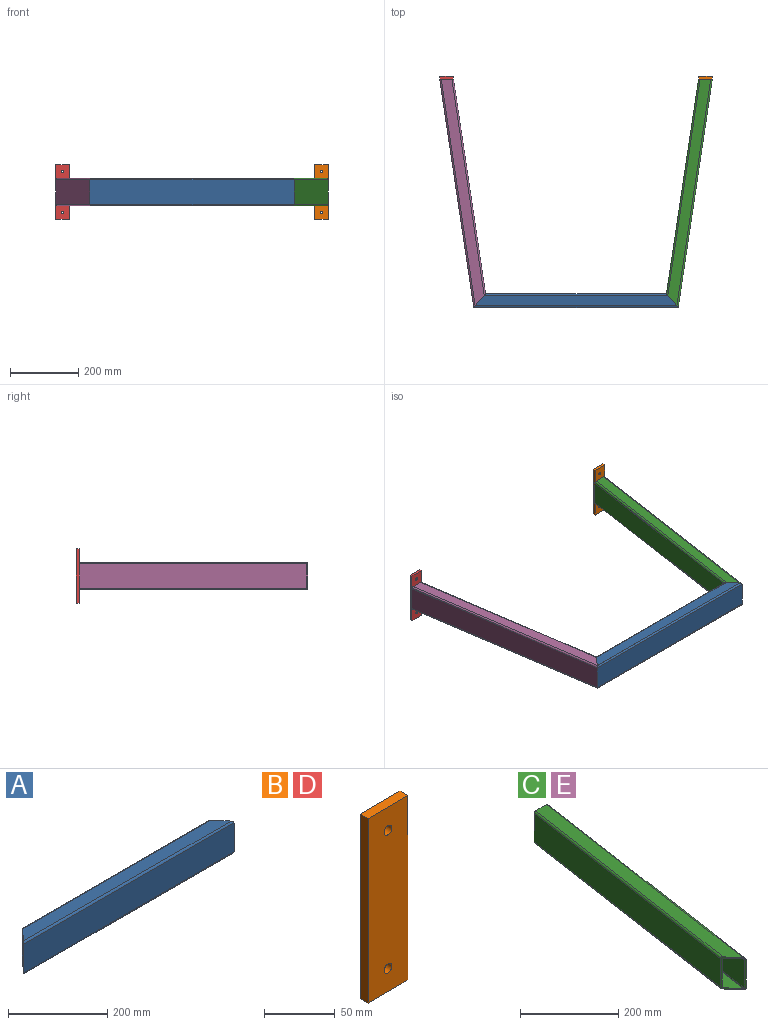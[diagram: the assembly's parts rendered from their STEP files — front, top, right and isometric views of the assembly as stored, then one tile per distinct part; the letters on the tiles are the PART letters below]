
ASSEMBLY  parts=5 mates=2
PART A: 18 faces, bbox 600x40x80 mm
  f0: cylinder r=4.5mm len=600mm, axis (-1,0,0), area 4221.2mm2, adj f2,f7,f8,f17
  f1: cylinder r=4.5mm len=600mm, axis (1,0,0), area 4221.2mm2, adj f2,f6,f8,f17
  f2: plane 600x71mm, normal (0,-1,0), area 42600mm2, adj f0,f1,f8,f17
  f3: cylinder r=4.5mm len=538.81mm, axis (1,0,0), area 3773.7mm2, adj f5,f7,f8,f17
  f4: cylinder r=4.5mm len=538.81mm, axis (-1,0,0), area 3773.7mm2, adj f5,f6,f8,f17
  f5: plane 531.05x71mm, normal (0,1,0), area 37704.8mm2, adj f3,f4,f8,f17
  f6: plane 592.24x31mm, normal (0,0,-1), area 17531.3mm2, adj f1,f4,f8,f17
  f7: plane 592.24x31mm, normal (0,0,1), area 17531.3mm2, adj f0,f3,f8,f17
  f8: plane 80x40mm, normal (-0.76,0.65,0), area 882.6mm2, adj f0,f1,f2,f3,f4,f5,f6,f7
  f9: cylinder r=1.5mm len=594.83mm, axis (1,0,0), area 1399.3mm2, adj f8,f11,f15,f17
  f10: cylinder r=1.5mm len=594.83mm, axis (-1,0,0), area 1399.3mm2, adj f8,f11,f16,f17
  f11: plane 594.83x71mm, normal (0,1,0), area 42232.9mm2, adj f8,f9,f10,f17
  f12: cylinder r=1.5mm len=538.81mm, axis (-1,0,0), area 1265.7mm2, adj f8,f14,f15,f17
  f13: cylinder r=1.5mm len=538.81mm, axis (1,0,0), area 1265.7mm2, adj f8,f14,f16,f17
  f14: plane 536.23x71mm, normal (0,-1,0), area 38072mm2, adj f8,f12,f13,f17
  f15: plane 592.24x31mm, normal (0,0,1), area 17531.3mm2, adj f8,f9,f12,f17
  f16: plane 592.24x31mm, normal (0,0,-1), area 17531.3mm2, adj f8,f10,f13,f17
  f17: plane 80x40mm, normal (0.76,0.65,0), area 882.6mm2, adj f0,f1,f2,f3,f4,f5,f6,f7
PART B: 8 faces, bbox 40x8x160 mm
  f0: plane 160x40mm, normal (0,-1,0), area 6299.5mm2, adj f1,f3,f4,f5,f6,f7
  f1: plane 160x8mm, normal (1,0,0), area 1280mm2, adj f0,f2,f4,f5
  f2: plane 160x40mm, normal (0,1,0), area 6299.5mm2, adj f1,f3,f4,f5,f6,f7
  f3: plane 160x8mm, normal (-1,0,0), area 1280mm2, adj f0,f2,f4,f5
  f4: plane 40x8mm, normal (0,0,1), area 320mm2, adj f0,f1,f2,f3
  f5: plane 40x8mm, normal (0,0,-1), area 320mm2, adj f0,f1,f2,f3
  f6: cylinder r=4mm len=8mm, axis (0,-1,0), area 201.1mm2, adj f0,f2
  f7: cylinder r=4mm len=8mm, axis (0,-1,0), area 201.1mm2, adj f0,f2
PART C: 18 faces, bbox 135x670.7x80 mm
  f0: plane 665.5x126.05mm, normal (0,0,1), area 20373.2mm2, adj f5,f9,f10,f17
  f1: plane 665.5x126.05mm, normal (0,0,-1), area 20373.2mm2, adj f5,f7,f8,f17
  f2: plane 665.5x126.05mm, normal (0,0,-1), area 20373.2mm2, adj f5,f15,f16,f17
  f3: plane 665.5x126.05mm, normal (0,0,1), area 20373.2mm2, adj f5,f13,f14,f17
  f4: plane 670x100mm, normal (0.99,-0.15,0), area 48096.9mm2, adj f5,f7,f9,f17
  f5: plane 80x40.44mm, normal (0,1,0), area 676mm2, adj f0,f1,f2,f3,f4,f6,f7,f8
  f6: plane 630x94.03mm, normal (-0.99,0.15,0), area 45225.5mm2, adj f5,f8,f10,f17
  f7: cylinder r=4.5mm len=670.66mm, axis (0.15,0.99,0), area 4776.7mm2, adj f1,f4,f5,f17
  f8: cylinder r=4.5mm len=635.16mm, axis (-0.15,-0.99,0), area 4514.2mm2, adj f1,f5,f6,f17
  f9: cylinder r=4.5mm len=670.66mm, axis (-0.15,-0.99,0), area 4776.7mm2, adj f0,f4,f5,f17
  f10: cylinder r=4.5mm len=635.16mm, axis (0.15,0.99,0), area 4514.2mm2, adj f0,f5,f6,f17
  f11: plane 667x99.55mm, normal (-0.99,0.15,0), area 47881.6mm2, adj f5,f13,f15,f17
  f12: plane 633x94.48mm, normal (0.99,-0.15,0), area 45440.8mm2, adj f5,f14,f16,f17
  f13: cylinder r=1.5mm len=667.22mm, axis (0.15,0.99,0), area 1587.7mm2, adj f3,f5,f11,f17
  f14: cylinder r=1.5mm len=634.72mm, axis (-0.15,-0.99,0), area 1509.3mm2, adj f3,f5,f12,f17
  f15: cylinder r=1.5mm len=667.22mm, axis (-0.15,-0.99,0), area 1587.7mm2, adj f2,f5,f11,f17
  f16: cylinder r=1.5mm len=634.72mm, axis (0.15,0.99,0), area 1509.3mm2, adj f2,f5,f12,f17
  f17: plane 80x40mm, normal (-0.76,-0.65,0), area 882.6mm2, adj f0,f1,f2,f3,f4,f6,f7,f8
PART D: same geometry as B
PART E: same geometry as C
PLACE A at identity fixed
PLACE B at identity
PLACE C at identity
PLACE D rot(axis=(0,1,0),180deg) t=(0,0,0)mm
PLACE E rot(axis=(0,-1,0),180deg) t=(0,0,0)mm
MATE fastened D.f0 <-> E.f5  axis (0,-1,0) through (-400,670,0)mm
MATE fastened E.f17 <-> A.f8  axis (0.76,-0.65,0) through (-296.12,4.5,35.5)mm
